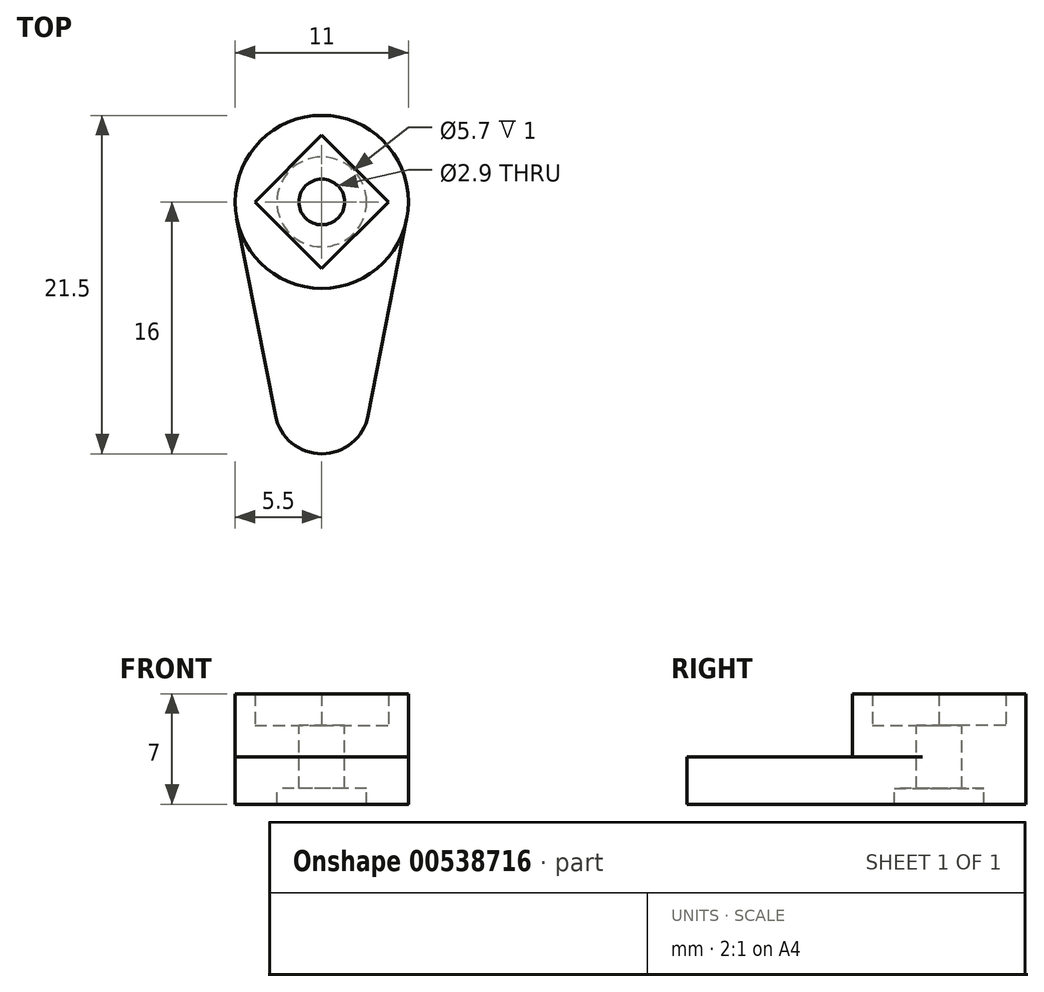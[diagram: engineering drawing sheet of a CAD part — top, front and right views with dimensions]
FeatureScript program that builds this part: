
annotation { "Feature Type Name" : "Feature", "Feature Type Description" : "" }
export const myFeature = defineFeature(function(context is Context, id is Id, definition is map)
    precondition{}
    {
        {
            var Q0;
            Q0=qCreatedBy(makeId("Top.planeOp"),FACE);
            var sketch = newSketch(context, id + "F0", { "sketchPlane" : qUnion([Q0])});
            skCircle(sketch, "E0.cCircle", {"center": v(0, 0) * mm, "radius": 3 * mm, "construction": true});
            skLineSegment(sketch, "E0.0", {"start": v(0, 4.24) * mm, "end": v(4.24, 0) * mm, "construction": true});
            skLineSegment(sketch, "E0.1", {"start": v(4.24, 0) * mm, "end": v(0, -4.24) * mm, "construction": true});
            skLineSegment(sketch, "E0.2", {"start": v(0, -4.24) * mm, "end": v(-4.24, 0) * mm, "construction": true});
            skLineSegment(sketch, "E0.3", {"start": v(-4.24, 0) * mm, "end": v(0, 4.24) * mm, "construction": true});
            skPoint(sketch, "E0.0.midPoint", {"position": v(2.12, 2.12) * mm});
            skCircle(sketch, "E1", {"center": v(0, 0) * mm, "radius": 5.5 * mm});
            skSolve(sketch);
        }
        {
            var Q0;
            Q0 = qSketchRegion(id + "F0", true);
            extrude(context, id + "F1", {"entities" : qUnion([Q0]), "oppositeDirection" : true, "depth" : 5 * mm, "offsetDistance" : 25 * mm, "hasSecondDirection" : true, "secondDirectionOppositeDirection" : false, "secondDirectionDepth" : 2 * mm});
        }
        {
            var Q0;
            Q0=qCreatedBy(makeId("Top.planeOp"),FACE);
            var sketch = newSketch(context, id + "F2", { "sketchPlane" : qUnion([Q0])});
            skCircle(sketch, "E2.cCircle", {"center": v(0, 0) * mm, "radius": 3 * mm, "construction": true});
            skLineSegment(sketch, "E2.0", {"start": v(0, 4.24) * mm, "end": v(4.24, 0) * mm});
            skLineSegment(sketch, "E2.1", {"start": v(4.24, 0) * mm, "end": v(0, -4.24) * mm});
            skLineSegment(sketch, "E2.2", {"start": v(0, -4.24) * mm, "end": v(-4.24, 0) * mm});
            skLineSegment(sketch, "E2.3", {"start": v(-4.24, 0) * mm, "end": v(0, 4.24) * mm});
            skPoint(sketch, "E2.0.midPoint", {"position": v(2.12, 2.12) * mm});
            skSolve(sketch);
        }
        {
            var Q0;
            Q0 = qSketchRegion(id + "F2", true);
            extrude(context, id + "F3", {"entities" : qUnion([Q0]), "operationType" : NewBodyOperationType.REMOVE, "depth" : 2 * mm, "offsetDistance" : 25 * mm});
        }
        {
            var Q0;
            Q0=qCreatedBy(makeId("Top.planeOp"),FACE);
            var sketch = newSketch(context, id + "F4", { "sketchPlane" : qUnion([Q0])});
            skArc(sketch, "E3", {"start": v(-2.94, -13.58) * mm, "mid": v(0, -16) * mm, "end": v(2.94, -13.58) * mm});
            skArc(sketch, "E4", {"start": v(5.4, -1.06) * mm, "mid": v(0, 5.5) * mm, "end": v(-5.4, -1.06) * mm});
            skLineSegment(sketch, "E5", {"start": v(2.94, -13.58) * mm, "end": v(5.6, 0) * mm});
            skLineSegment(sketch, "E6", {"start": v(-2.94, -13.58) * mm, "end": v(-5.6, 0) * mm});
            skSolve(sketch);
        }
        {
            var Q0;
            {var subQ0=sQuery(id+"F4.wireOp",EDGE,"E3");Q0=makeQuery(id+"F4.imprint","IMPRINT",FACE,{"disambiguationData":[TD([[makeQuery(id+"F4.imprint","IMPRINT",EDGE,{"derivedFrom":subQ0}),1.0]])]});}
            extrude(context, id + "F5", {"entities" : qUnion([Q0]), "operationType" : NewBodyOperationType.ADD, "oppositeDirection" : true, "depth" : 5 * mm, "offsetDistance" : 25 * mm, "hasSecondDirection" : true, "secondDirectionOppositeDirection" : true, "secondDirectionDepth" : 2 * mm});
        }
        {
            var Q0;
            Q0=qCreatedBy(makeId("Top.planeOp"),FACE);
            var sketch = newSketch(context, id + "F6", { "sketchPlane" : qUnion([Q0])});
            skCircle(sketch, "E7", {"center": v(0, 0) * mm, "radius": 2.85 * mm});
            skSolve(sketch);
        }
        {
            var Q0;
            Q0 = qSketchRegion(id + "F6", true);
            extrude(context, id + "F7", {"entities" : qUnion([Q0]), "operationType" : NewBodyOperationType.REMOVE, "oppositeDirection" : true, "depth" : 25 * mm, "offsetDistance" : 25 * mm, "hasSecondDirection" : true, "secondDirectionOppositeDirection" : true, "secondDirectionDepth" : 4 * mm});
        }
        {
            var Q0;
            Q0=qCreatedBy(makeId("Top.planeOp"),FACE);
            var sketch = newSketch(context, id + "F8", { "sketchPlane" : qUnion([Q0])});
            skCircle(sketch, "E8", {"center": v(0, 0) * mm, "radius": 1.45 * mm});
            skSolve(sketch);
        }
        {
            var Q0;
            Q0 = qSketchRegion(id + "F8", true);
            extrude(context, id + "F9", {"entities" : qUnion([Q0]), "operationType" : NewBodyOperationType.REMOVE, "oppositeDirection" : true, "depth" : 25 * mm, "offsetDistance" : 25 * mm, "hasSecondDirection" : true, "secondDirectionOppositeDirection" : false, "secondDirectionDepth" : 25 * mm});
        }
    });
